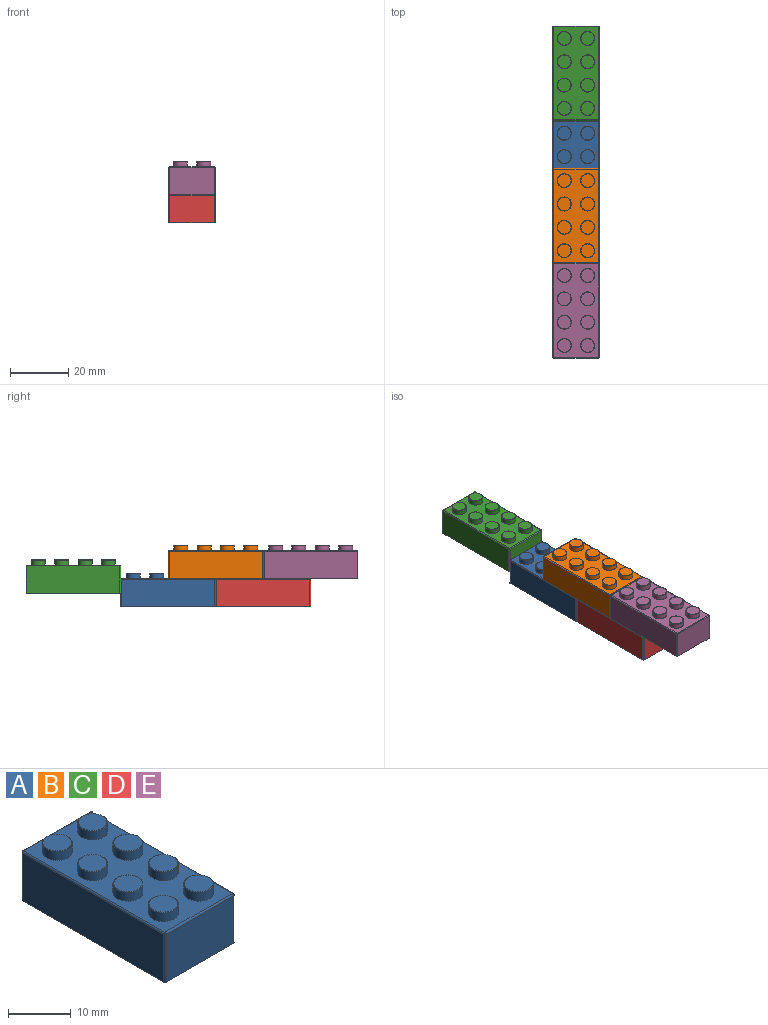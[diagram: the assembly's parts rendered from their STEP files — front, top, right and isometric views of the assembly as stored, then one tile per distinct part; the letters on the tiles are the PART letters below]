
ASSEMBLY  parts=5 mates=1
PART A: 128 faces, bbox 15.8x32.5x11.4 mm
  f0: plane 13.85x8.1mm, normal (-1,0,0), area 112.2mm2, adj f13,f73,f76,f79
  f1: plane 13.85x12.8mm, normal (0,0,-1), area 95.9mm2, adj f63,f68,f69,f74,f75,f79,f98,f102
  f2: cylinder r=3.25mm len=8.1mm, axis (0,0,-1), area 69.2mm2, adj f13,f62,f67,f68
  f3: plane 13.85x8.1mm, normal (1,0,0), area 112.2mm2, adj f13,f80,f82,f83
  f4: cylinder r=3.25mm len=8.1mm, axis (0,0,-1), area 69.2mm2, adj f13,f85,f90,f91
  f5: plane 4.8x4.8mm, normal (0,0,-1), area 18.1mm2, adj f7
  f6: plane 4.8x4.8mm, normal (0,0,-1), area 18.1mm2, adj f10
  f7: cylinder r=2.4mm len=8.4mm, axis (0,0,-1), area 126.7mm2, adj f5,f9
  f8: cylinder r=3.25mm len=8.1mm, axis (0,0,-1), area 165.4mm2, adj f9,f98
  f9: plane 6.5x6.5mm, normal (0,0,-1), area 15.1mm2, adj f7,f8
  f10: cylinder r=2.4mm len=8.4mm, axis (0,0,-1), area 126.7mm2, adj f6,f12
  f11: cylinder r=3.25mm len=8.1mm, axis (0,0,-1), area 165.4mm2, adj f12,f99
  f12: plane 6.5x6.5mm, normal (0,0,-1), area 15.1mm2, adj f10,f11
  f13: plane 32.5x15.8mm, normal (0,0,-1), area 133.7mm2, adj f0,f2,f3,f4,f14,f15,f16,f17
  f14: plane 31.9x9.3mm, normal (1,0,0), area 296.7mm2, adj f13,f110,f116,f119
  f15: plane 15.2x9.3mm, normal (0,1,0), area 141.4mm2, adj f13,f113,f117,f119
  f16: plane 31.9x9.3mm, normal (-1,0,0), area 296.7mm2, adj f13,f108,f112,f113
  f17: plane 15.2x9.3mm, normal (0,-1,0), area 141.4mm2, adj f13,f108,f110,f111
  f18: plane 31.9x15.2mm, normal (0,0,1), area 340.1mm2, adj f19,f21,f23,f25,f27,f29,f31,f33
  f19: cylinder r=2.4mm len=4.8mm, axis (0,0,-1), area 25.6mm2, adj f18,f127
  f20: plane 4.6x4.6mm, normal (0,0,1), area 16.6mm2, adj f127
  f21: cylinder r=2.4mm len=4.8mm, axis (0,0,-1), area 25.6mm2, adj f18,f126
  f22: plane 4.6x4.6mm, normal (0,0,1), area 16.6mm2, adj f126
  f23: cylinder r=2.4mm len=4.8mm, axis (0,0,-1), area 25.6mm2, adj f18,f125
  f24: plane 4.6x4.6mm, normal (0,0,1), area 16.6mm2, adj f125
  f25: cylinder r=2.4mm len=4.8mm, axis (0,0,-1), area 25.6mm2, adj f18,f124
  f26: plane 4.6x4.6mm, normal (0,0,1), area 16.6mm2, adj f124
  f27: cylinder r=2.4mm len=4.8mm, axis (0,0,-1), area 25.6mm2, adj f18,f123
  f28: plane 4.6x4.6mm, normal (0,0,1), area 16.6mm2, adj f123
  f29: cylinder r=2.4mm len=4.8mm, axis (0,0,-1), area 25.6mm2, adj f18,f122
  f30: plane 4.6x4.6mm, normal (0,0,1), area 16.6mm2, adj f122
  f31: cylinder r=2.4mm len=4.8mm, axis (0,0,-1), area 25.6mm2, adj f18,f121
  f32: plane 4.6x4.6mm, normal (0,0,1), area 16.6mm2, adj f121
  f33: cylinder r=2.4mm len=4.8mm, axis (0,0,-1), area 25.6mm2, adj f18,f120
  f34: plane 4.6x4.6mm, normal (0,0,1), area 16.6mm2, adj f120
  f35: plane 13.85x8.1mm, normal (-1,0,0), area 112.2mm2, adj f13,f88,f94,f97
  f36: plane 12.8x8.1mm, normal (0,-1,0), area 103.7mm2, adj f13,f82,f88,f89
  f37: plane 13.85x8.1mm, normal (1,0,0), area 112.2mm2, adj f13,f64,f69,f70
  f38: plane 12.8x8.1mm, normal (0,1,0), area 103.7mm2, adj f13,f70,f75,f76
  f39: plane 13.85x12.8mm, normal (0,0,-1), area 95.9mm2, adj f83,f84,f89,f90,f94,f95,f99,f100
  f40: cylinder r=1.2mm len=2.4mm, axis (0,0,-1), area 11.3mm2, adj f41,f107
  f41: plane 2.4x2.4mm, normal (0,0,-1), area 4.5mm2, adj f40
  f42: cylinder r=1.2mm len=2.4mm, axis (0,0,-1), area 11.3mm2, adj f43,f106
  f43: plane 2.4x2.4mm, normal (0,0,-1), area 4.5mm2, adj f42
  f44: cylinder r=1.2mm len=2.4mm, axis (0,0,-1), area 11.3mm2, adj f45,f105
  f45: plane 2.4x2.4mm, normal (0,0,-1), area 4.5mm2, adj f44
  f46: cylinder r=1.2mm len=2.4mm, axis (0,0,-1), area 11.3mm2, adj f47,f104
  f47: plane 2.4x2.4mm, normal (0,0,-1), area 4.5mm2, adj f46
  f48: cylinder r=1.2mm len=2.4mm, axis (0,0,-1), area 11.3mm2, adj f49,f103
  f49: plane 2.4x2.4mm, normal (0,0,-1), area 4.5mm2, adj f48
  f50: cylinder r=1.2mm len=2.4mm, axis (0,0,-1), area 11.3mm2, adj f51,f102
  f51: plane 2.4x2.4mm, normal (0,0,-1), area 4.5mm2, adj f50
  f52: cylinder r=1.2mm len=2.4mm, axis (0,0,-1), area 11.3mm2, adj f53,f101
  f53: plane 2.4x2.4mm, normal (0,0,-1), area 4.5mm2, adj f52
  f54: cylinder r=1.2mm len=2.4mm, axis (0,0,-1), area 11.3mm2, adj f55,f100
  f55: plane 2.4x2.4mm, normal (0,0,-1), area 4.5mm2, adj f54
  f56: cylinder r=2.4mm len=8.4mm, axis (0,0,-1), area 126.7mm2, adj f13,f57
  f57: plane 4.8x4.8mm, normal (0,0,-1), area 18.1mm2, adj f56
  f58: plane 8.1x2.97mm, normal (0,-1,0), area 24mm2, adj f13,f62,f63,f64
  f59: plane 8.1x2.97mm, normal (0,1,0), area 24mm2, adj f13,f80,f84,f85
  f60: plane 8.1x2.97mm, normal (0,-1,0), area 24mm2, adj f13,f67,f73,f74
  f61: plane 8.1x2.97mm, normal (0,1,0), area 24mm2, adj f13,f91,f95,f97
  f62: cylinder r=0.3mm len=8.1mm, axis (0,0,-1), area 3.2mm2, adj f2,f13,f58,f65
  f63: cylinder r=0.3mm len=2.97mm, axis (-1,0,0), area 1.4mm2, adj f1,f58,f65,f66
  f64: cylinder r=0.3mm len=8.1mm, axis (0,0,-1), area 3.8mm2, adj f13,f37,f58,f66
  f65: sphere r=0.3mm, area 0.1mm2, adj f62,f63,f68
  f66: sphere r=0.3mm, area 0.1mm2, adj f63,f64,f69
  f67: cylinder r=0.3mm len=8.1mm, axis (0,0,-1), area 3.2mm2, adj f2,f13,f60,f71
  f68: torus R=3.55mm, axis (0,0,1), area 4.2mm2, adj f1,f2,f65,f71
  f69: cylinder r=0.3mm len=13.85mm, axis (0,-1,0), area 6.5mm2, adj f1,f37,f66,f72
  f70: cylinder r=0.3mm len=8.1mm, axis (0,0,-1), area 3.8mm2, adj f13,f37,f38,f72
  f71: sphere r=0.3mm, area 0.1mm2, adj f67,f68,f74
  f72: sphere r=0.3mm, area 0.1mm2, adj f69,f70,f75
  f73: cylinder r=0.3mm len=8.1mm, axis (0,0,1), area 3.8mm2, adj f0,f13,f60,f77
  f74: cylinder r=0.3mm len=2.97mm, axis (-1,0,0), area 1.4mm2, adj f1,f60,f71,f77
  f75: cylinder r=0.3mm len=12.8mm, axis (1,0,0), area 6mm2, adj f1,f38,f72,f78
  f76: cylinder r=0.3mm len=8.1mm, axis (0,0,1), area 3.8mm2, adj f0,f13,f38,f78
  f77: sphere r=0.3mm, area 0.1mm2, adj f73,f74,f79
  f78: sphere r=0.3mm, area 0.1mm2, adj f75,f76,f79
  f79: cylinder r=0.3mm len=13.85mm, axis (0,1,0), area 6.5mm2, adj f0,f1,f77,f78
  f80: cylinder r=0.3mm len=8.1mm, axis (0,0,1), area 3.8mm2, adj f3,f13,f59,f81
  f81: sphere r=0.3mm, area 0.1mm2, adj f80,f83,f84
  f82: cylinder r=0.3mm len=8.1mm, axis (0,0,1), area 3.8mm2, adj f3,f13,f36,f86
  f83: cylinder r=0.3mm len=13.85mm, axis (0,-1,0), area 6.5mm2, adj f3,f39,f81,f86
  f84: cylinder r=0.3mm len=2.97mm, axis (1,0,0), area 1.4mm2, adj f39,f59,f81,f87
  f85: cylinder r=0.3mm len=8.1mm, axis (0,0,-1), area 3.2mm2, adj f4,f13,f59,f87
  f86: sphere r=0.3mm, area 0.1mm2, adj f82,f83,f89
  f87: sphere r=0.3mm, area 0.1mm2, adj f84,f85,f90
  f88: cylinder r=0.3mm len=8.1mm, axis (0,0,-1), area 3.8mm2, adj f13,f35,f36,f92
  f89: cylinder r=0.3mm len=12.8mm, axis (-1,0,0), area 6mm2, adj f36,f39,f86,f92
  f90: torus R=3.55mm, axis (0,0,1), area 4.2mm2, adj f4,f39,f87,f93
  f91: cylinder r=0.3mm len=8.1mm, axis (0,0,-1), area 3.2mm2, adj f4,f13,f61,f93
  f92: sphere r=0.3mm, area 0.1mm2, adj f88,f89,f94
  f93: sphere r=0.3mm, area 0.1mm2, adj f90,f91,f95
  f94: cylinder r=0.3mm len=13.85mm, axis (0,1,0), area 6.5mm2, adj f35,f39,f92,f96
  f95: cylinder r=0.3mm len=2.97mm, axis (1,0,0), area 1.4mm2, adj f39,f61,f93,f96
  f96: sphere r=0.3mm, area 0.1mm2, adj f94,f95,f97
  f97: cylinder r=0.3mm len=8.1mm, axis (0,0,-1), area 3.8mm2, adj f13,f35,f61,f96
  f98: torus R=3.55mm, axis (0,0,1), area 9.9mm2, adj f1,f8
  f99: torus R=3.55mm, axis (0,0,1), area 9.9mm2, adj f11,f39
  f100: torus R=1.5mm, axis (0,0,1), area 3.9mm2, adj f39,f54
  f101: torus R=1.5mm, axis (0,0,1), area 3.9mm2, adj f39,f52
  f102: torus R=1.5mm, axis (0,0,1), area 3.9mm2, adj f1,f50
  f103: torus R=1.5mm, axis (0,0,1), area 3.9mm2, adj f1,f48
  f104: torus R=1.5mm, axis (0,0,1), area 3.9mm2, adj f39,f46
  f105: torus R=1.5mm, axis (0,0,1), area 3.9mm2, adj f39,f44
  f106: torus R=1.5mm, axis (0,0,1), area 3.9mm2, adj f1,f42
  f107: torus R=1.5mm, axis (0,0,1), area 3.9mm2, adj f1,f40
  f108: cylinder r=0.3mm len=9.3mm, axis (0,0,1), area 4.4mm2, adj f13,f16,f17,f109
  f109: sphere r=0.3mm, area 0.1mm2, adj f108,f111,f112
  f110: cylinder r=0.3mm len=9.3mm, axis (0,0,-1), area 4.4mm2, adj f13,f14,f17,f114
  f111: cylinder r=0.3mm len=15.2mm, axis (-1,0,0), area 7.2mm2, adj f17,f18,f109,f114
  f112: cylinder r=0.3mm len=31.9mm, axis (0,1,0), area 15mm2, adj f16,f18,f109,f115
  f113: cylinder r=0.3mm len=9.3mm, axis (0,0,-1), area 4.4mm2, adj f13,f15,f16,f115
  f114: sphere r=0.3mm, area 0.1mm2, adj f110,f111,f116
  f115: sphere r=0.3mm, area 0.1mm2, adj f112,f113,f117
  f116: cylinder r=0.3mm len=31.9mm, axis (0,-1,0), area 15mm2, adj f14,f18,f114,f118
  f117: cylinder r=0.3mm len=15.2mm, axis (1,0,0), area 7.2mm2, adj f15,f18,f115,f118
  f118: sphere r=0.3mm, area 0.1mm2, adj f116,f117,f119
  f119: cylinder r=0.3mm len=9.3mm, axis (0,0,1), area 4.4mm2, adj f13,f14,f15,f118
  f120: torus R=2.3mm, axis (0,0,1), area 2.3mm2, adj f33,f34
  f121: torus R=2.3mm, axis (0,0,1), area 2.3mm2, adj f31,f32
  f122: torus R=2.3mm, axis (0,0,1), area 2.3mm2, adj f29,f30
  f123: torus R=2.3mm, axis (0,0,1), area 2.3mm2, adj f27,f28
  f124: torus R=2.3mm, axis (0,0,1), area 2.3mm2, adj f25,f26
  f125: torus R=2.3mm, axis (0,0,1), area 2.3mm2, adj f23,f24
  f126: torus R=2.3mm, axis (0,0,1), area 2.3mm2, adj f21,f22
  f127: torus R=2.3mm, axis (0,0,1), area 2.3mm2, adj f19,f20
PART B: same geometry as A
PART C: same geometry as A
PART D: same geometry as A
PART E: same geometry as A
PLACE A at identity fixed
PLACE B t=(0,-16.25,9.6)mm
PLACE C t=(0,32.5,4.65)mm
PLACE D t=(0,-32.5,0)mm
PLACE E t=(0,-48.75,9.6)mm
MATE fastened C.f17 <-> A.f15  axis (0,-1,0) through (0,16.25,4.65)mm
